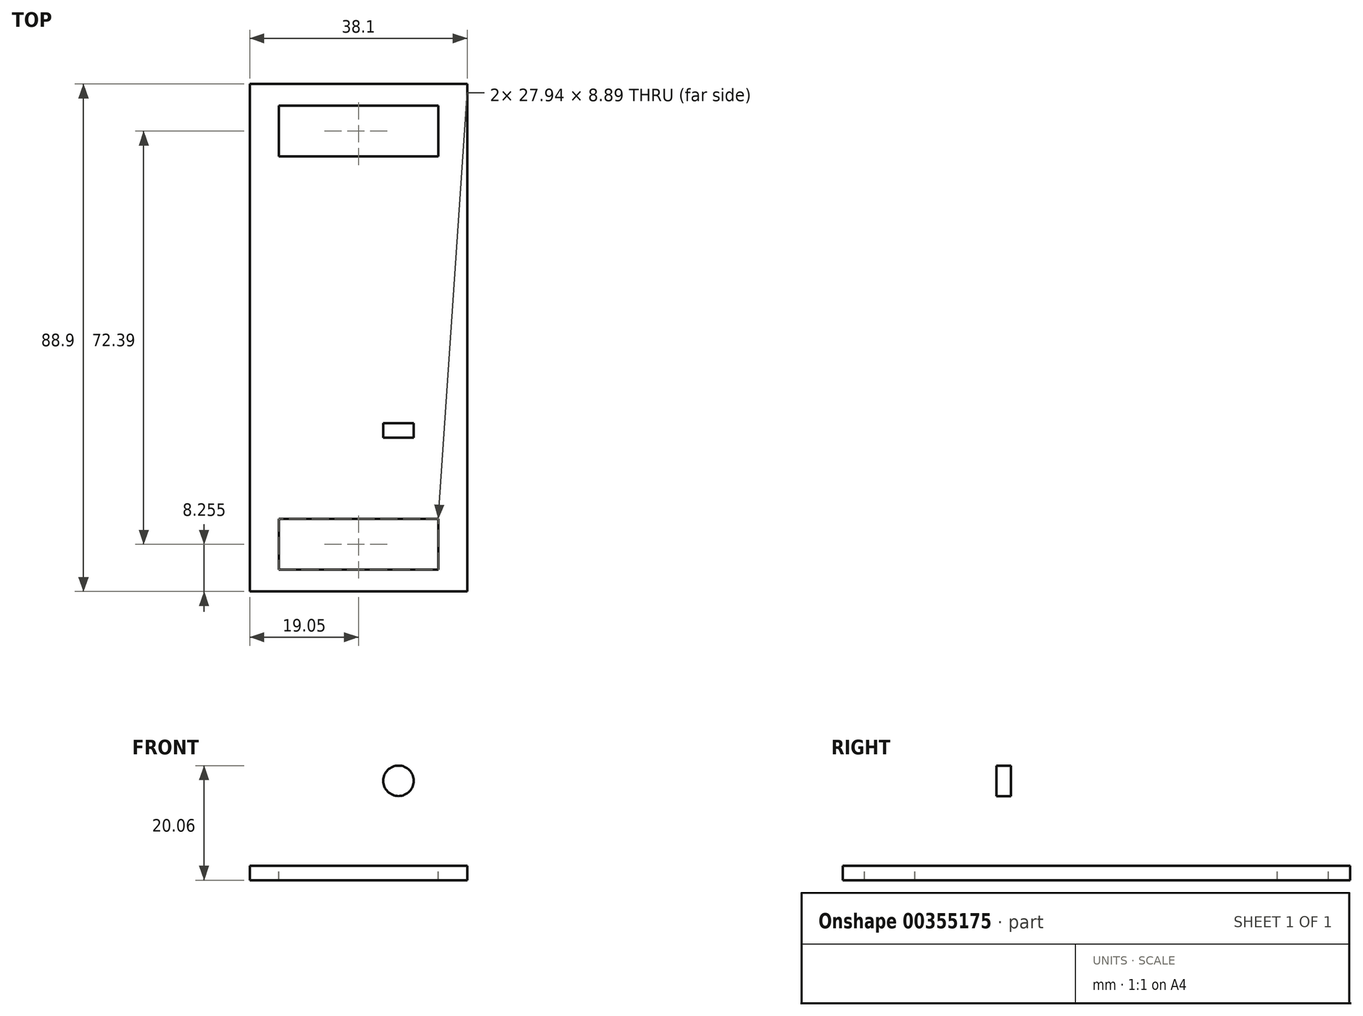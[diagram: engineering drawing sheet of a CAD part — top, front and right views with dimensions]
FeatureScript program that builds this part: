
annotation { "Feature Type Name" : "Feature", "Feature Type Description" : "" }
export const myFeature = defineFeature(function(context is Context, id is Id, definition is map)
    precondition{}
    {
        {
            var Q0;
            Q0=qCreatedBy(makeId("Top.planeOp"),FACE);
            var sketch = newSketch(context, id + "F0", { "sketchPlane" : qUnion([Q0])});
            skLineSegment(sketch, "E0.bottom", {"start": v(0, 0) * mm, "end": v(38.1, 0) * mm});
            skLineSegment(sketch, "E0.top", {"start": v(0, 88.9) * mm, "end": v(38.1, 88.9) * mm});
            skLineSegment(sketch, "E0.left", {"start": v(0, 0) * mm, "end": v(0, 88.9) * mm});
            skLineSegment(sketch, "E0.right", {"start": v(38.1, 0) * mm, "end": v(38.1, 88.9) * mm});
            skLineSegment(sketch, "E1", {"start": v(19.05, 88.9) * mm, "end": v(19.05, 0) * mm, "construction": true});
            skLineSegment(sketch, "E2", {"start": v(19.05, 55.1) * mm, "end": v(38.08, 55.1) * mm, "construction": true});
            skLineSegment(sketch, "E3.bottom", {"start": v(19.05, 65.17) * mm, "end": v(29.05, 65.17) * mm});
            skLineSegment(sketch, "E3.top", {"start": v(19.05, 60.1) * mm, "end": v(29.05, 60.1) * mm});
            skLineSegment(sketch, "E3.left", {"start": v(19.05, 65.17) * mm, "end": v(19.05, 60.1) * mm});
            skLineSegment(sketch, "E3.right", {"start": v(29.05, 65.17) * mm, "end": v(29.05, 60.1) * mm});
            skLineSegment(sketch, "E4.MirrorCS", {"start": v(19.05, 45.01) * mm, "end": v(19.05, 50.1) * mm});
            skLineSegment(sketch, "E5.MirrorCS", {"start": v(19.05, 45.01) * mm, "end": v(29.05, 45.01) * mm});
            skLineSegment(sketch, "E6.MirrorCS", {"start": v(29.05, 45.01) * mm, "end": v(29.05, 50.1) * mm});
            skLineSegment(sketch, "E7.MirrorCS", {"start": v(19.05, 50.1) * mm, "end": v(29.05, 50.1) * mm});
            skLineSegment(sketch, "E8.bottom", {"start": v(31.89, 29.5) * mm, "end": v(6.49, 29.5) * mm});
            skLineSegment(sketch, "E8.top", {"start": v(31.89, 26.96) * mm, "end": v(6.49, 26.96) * mm});
            skLineSegment(sketch, "E8.left", {"start": v(31.89, 29.5) * mm, "end": v(31.89, 26.96) * mm});
            skLineSegment(sketch, "E8.right", {"start": v(6.49, 29.5) * mm, "end": v(6.49, 26.96) * mm});
            skLineSegment(sketch, "E9", {"start": v(31.89, 28.23) * mm, "end": v(19.19, 28.23) * mm, "construction": true});
            skPoint(sketch, "E9.endSnap0", {"position": v(19.19, 29.5) * mm});
            skLineSegment(sketch, "E10", {"start": v(19.19, 28.23) * mm, "end": v(6.49, 28.23) * mm, "construction": true});
            skSolve(sketch);
        }
        {
            var Q0;
            Q0=qCreatedBy(makeId("Top.planeOp"),FACE);
            var sketch = newSketch(context, id + "F1", { "sketchPlane" : qUnion([Q0])});
            skLineSegment(sketch, "E11.0", {"start": v(38.1, 0) * mm, "end": v(38.1, 88.9) * mm});
            skLineSegment(sketch, "E12.0", {"start": v(0, 88.9) * mm, "end": v(38.1, 88.9) * mm});
            skLineSegment(sketch, "E13.0", {"start": v(0, 0) * mm, "end": v(0, 88.9) * mm});
            skLineSegment(sketch, "E14.0", {"start": v(0, 0) * mm, "end": v(38.1, 0) * mm});
            skSolve(sketch);
        }
        {
            var Q0;
            Q0 = qSketchRegion(id + "F1", true);
            extrude(context, id + "F2", {"entities" : qUnion([Q0]), "oppositeDirection" : true, "depth" : 2.54 * mm});
        }
        {
            var Q0;
            Q0=makeQuery(id+"F0.imprint","IMPRINT",FACE,{"disambiguationData":[TD([[makeQuery(id+"F0.imprint","IMPRINT",EDGE,{"derivedFrom":sQuery(id+"F0.wireOp",EDGE,"E3.bottom")}),-1.0]])]});
            var Q1;
            Q1=makeQuery(id+"F0.imprint","IMPRINT",FACE,{"disambiguationData":[TD([[makeQuery(id+"F0.imprint","IMPRINT",EDGE,{"derivedFrom":sQuery(id+"F0.wireOp",EDGE,"E4.MirrorCS")}),-1.0]])]});
            var Q2;
            Q2=makeQuery(id+"F0.imprint","IMPRINT",FACE,{"disambiguationData":[TD([[makeQuery(id+"F0.imprint","IMPRINT",EDGE,{"derivedFrom":sQuery(id+"F0.wireOp",EDGE,"E8.bottom")}),1.0]])]});
            extrude(context, id + "F3", {"entities" : qUnion([Q0, Q1, Q2]), "operationType" : NewBodyOperationType.ADD, "depth" : 6.35 * mm});
        }
        {
            var Q0;
            Q0=makeQuery(id+"F3.opExtrude","SWEPT_FACE",FACE,{"disambiguationData":[OSD([sQuery(id+"F0.wireOp",EDGE,"E7.MirrorCS")])]});
            var sketch = newSketch(context, id + "F4", { "sketchPlane" : qUnion([Q0])});
            skLineSegment(sketch, "E15", {"start": v(-29.05, 5.35) * mm, "end": v(-19.05, 5.35) * mm});
            skLineSegment(sketch, "E16", {"start": v(-19.05, 5.35) * mm, "end": v(-19.05, 3.35) * mm});
            skLineSegment(sketch, "E17", {"start": v(-19.05, 3.35) * mm, "end": v(-29.05, 3.35) * mm});
            skLineSegment(sketch, "E18", {"start": v(-29.05, 3.35) * mm, "end": v(-29.05, 5.35) * mm});
            skSolve(sketch);
        }
        {
            var Q0;
            Q0 = qSketchRegion(id + "F4", true);
            extrude(context, id + "F5", {"entities" : qUnion([Q0]), "operationType" : NewBodyOperationType.REMOVE, "oppositeDirection" : true, "depth" : .5 * mm});
        }
        {
            var Q0;
            Q0=makeQuery(id+"F3.opExtrude","SWEPT_FACE",FACE,{"disambiguationData":[OSD([sQuery(id+"F0.wireOp",EDGE,"E3.top")])]});
            var sketch = newSketch(context, id + "F6", { "sketchPlane" : qUnion([Q0])});
            skLineSegment(sketch, "E19.0.0", {"start": v(29.05, 3.35) * mm, "end": v(19.05, 3.35) * mm});
            skLineSegment(sketch, "E19.0.1", {"start": v(19.05, 3.35) * mm, "end": v(19.05, 5.35) * mm});
            skLineSegment(sketch, "E19.0.2", {"start": v(19.05, 5.35) * mm, "end": v(29.05, 5.35) * mm});
            skLineSegment(sketch, "E19.0.3", {"start": v(29.05, 5.35) * mm, "end": v(29.05, 3.35) * mm});
            skSolve(sketch);
        }
        {
            var Q0;
            Q0 = qSketchRegion(id + "F6", true);
            extrude(context, id + "F7", {"entities" : qUnion([Q0]), "operationType" : NewBodyOperationType.REMOVE, "oppositeDirection" : true, "depth" : .5 * mm});
        }
        {
            var Q0;
            Q0=makeQuery(id+"F3.opExtrude","CAP_FACE",FACE,{"disambiguationData":[OSD([sQuery(id+"F0.wireOp",EDGE,"E8.bottom"),sQuery(id+"F0.wireOp",EDGE,"E8.top"),sQuery(id+"F0.wireOp",EDGE,"E8.left"),sQuery(id+"F0.wireOp",EDGE,"E8.right")])],"isStart":false});
            extrude(context, id + "F8", {"entities" : qUnion([Q0]), "operationType" : NewBodyOperationType.ADD, "depth" : 12.7 * mm});
        }
        {
            var Q0;
            Q0=makeQuery(id+"F3.opExtrude","SWEPT_FACE",FACE,{"disambiguationData":[OSD([sQuery(id+"F0.wireOp",EDGE,"E8.top")])]});
            var sketch = newSketch(context, id + "F9", { "sketchPlane" : qUnion([Q0])});
            skLineSegment(sketch, "E20", {"start": v(19.19, 6.35) * mm, "end": v(19.19, 0) * mm, "construction": true});
            skCircle(sketch, "E21", {"center": v(12.3, 14.86) * mm, "radius": 2.67 * mm});
            skCircle(sketch, "E22.MirrorC", {"center": v(26.07, 14.86) * mm, "radius": 2.67 * mm});
            skSolve(sketch);
        }
        {
            var Q0;
            Q0=makeQuery(id+"F9.imprint","IMPRINT",FACE,{"disambiguationData":[TD([[makeQuery(id+"F9.imprint","IMPRINT",EDGE,{"derivedFrom":sQuery(id+"F9.wireOp",EDGE,"E21")}),1.0]])]});
            var Q1;
            Q1=makeQuery(id+"F9.imprint","IMPRINT",FACE,{"disambiguationData":[TD([[makeQuery(id+"F9.imprint","IMPRINT",EDGE,{"derivedFrom":sQuery(id+"F9.wireOp",EDGE,"E22.MirrorC")}),-1.0]])]});
            extrude(context, id + "F10", {"entities" : qUnion([Q0, Q1]), "operationType" : NewBodyOperationType.REMOVE, "endBound" : BoundingType.THROUGH_ALL, "oppositeDirection" : true, "depth" : 25.4 * mm});
        }
        {
            var Q0;
            Q0=makeQuery(id+"F2.opExtrude","CAP_FACE",FACE,{"disambiguationData":[OSD([sQuery(id+"F1.wireOp",EDGE,"E11.0"),sQuery(id+"F1.wireOp",EDGE,"E12.0"),sQuery(id+"F1.wireOp",EDGE,"E13.0"),sQuery(id+"F1.wireOp",EDGE,"E14.0")])],"isStart":true});
            var sketch = newSketch(context, id + "F11", { "sketchPlane" : qUnion([Q0])});
            skLineSegment(sketch, "E23", {"start": v(0, 44.45) * mm, "end": v(38.1, 44.45) * mm, "construction": true});
            skLineSegment(sketch, "E24.bottom", {"start": v(5.08, 85.1) * mm, "end": v(33.02, 85.1) * mm});
            skLineSegment(sketch, "E24.top", {"start": v(5.08, 76.2) * mm, "end": v(33.02, 76.2) * mm});
            skLineSegment(sketch, "E24.left", {"start": v(5.08, 85.1) * mm, "end": v(5.08, 76.2) * mm});
            skLineSegment(sketch, "E24.right", {"start": v(33.02, 85.1) * mm, "end": v(33.02, 76.2) * mm});
            skLineSegment(sketch, "E25", {"start": v(19.05, 88.9) * mm, "end": v(19.05, 0) * mm, "construction": true});
            skPoint(sketch, "E25.endSnap0", {"position": v(19.05, 85.1) * mm});
            skPoint(sketch, "E26.MirrorP", {"position": v(19.05, 3.8) * mm});
            skLineSegment(sketch, "E27.MirrorCS", {"start": v(5.08, 3.8) * mm, "end": v(33.02, 3.8) * mm});
            skLineSegment(sketch, "E28.MirrorCS", {"start": v(5.08, 12.7) * mm, "end": v(33.02, 12.7) * mm});
            skLineSegment(sketch, "E29.MirrorCS", {"start": v(5.08, 3.8) * mm, "end": v(5.08, 12.7) * mm});
            skLineSegment(sketch, "E30.MirrorCS", {"start": v(33.02, 3.8) * mm, "end": v(33.02, 12.7) * mm});
            skSolve(sketch);
        }
        {
            var Q0;
            Q0 = qSketchRegion(id + "F11", true);
            extrude(context, id + "F12", {"entities" : qUnion([Q0]), "operationType" : NewBodyOperationType.REMOVE, "oppositeDirection" : true, "depth" : 25.4 * mm});
        }
    });
